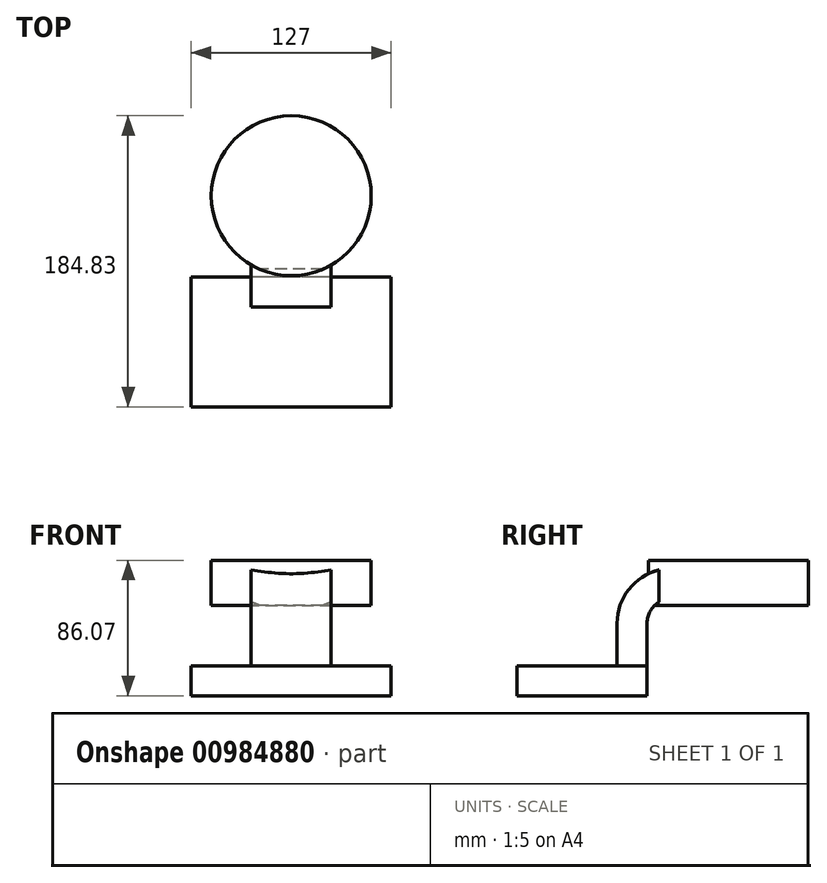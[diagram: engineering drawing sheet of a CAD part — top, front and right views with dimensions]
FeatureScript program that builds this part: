
annotation { "Feature Type Name" : "Feature", "Feature Type Description" : "" }
export const myFeature = defineFeature(function(context is Context, id is Id, definition is map)
    precondition{}
    {
        {
            var Q0;
            Q0=qCreatedBy(makeId("Right.planeOp"),FACE);
            var sketch = newSketch(context, id + "F0", { "sketchPlane" : qUnion([Q0])});
            skLineSegment(sketch, "E0.bottom", {"start": v(-41.28, 9.52) * mm, "end": v(41.28, 9.53) * mm});
            skLineSegment(sketch, "E0.top", {"start": v(-41.27, -9.52) * mm, "end": v(41.28, -9.52) * mm});
            skLineSegment(sketch, "E0.left", {"start": v(-41.28, 9.52) * mm, "end": v(-41.28, -9.52) * mm});
            skLineSegment(sketch, "E0.right", {"start": v(41.27, 9.53) * mm, "end": v(41.28, -9.52) * mm});
            skPoint(sketch, "E0.middle", {"position": v(0, 0) * mm});
            skLineSegment(sketch, "E1.bottom", {"start": v(143.56, 47.96) * mm, "end": v(92.76, 47.96) * mm});
            skLineSegment(sketch, "E1.top", {"start": v(143.56, 76.54) * mm, "end": v(92.76, 76.54) * mm});
            skLineSegment(sketch, "E1.left", {"start": v(143.56, 47.96) * mm, "end": v(143.56, 76.54) * mm});
            skLineSegment(sketch, "E1.right", {"start": v(92.76, 47.96) * mm, "end": v(92.76, 76.54) * mm});
            skPoint(sketch, "E1.middle", {"position": v(118.16, 62.25) * mm});
            skLineSegment(sketch, "E2", {"start": v(41.27, 9.53) * mm, "end": v(41.27, 36.51) * mm});
            skArc(sketch, "E3", {"start": v(41.27, 36.51) * mm, "mid": v(45.92, 47.74) * mm, "end": v(57.15, 52.39) * mm});
            skPoint(sketch, "E4.startSnap0", {"position": v(57.15, 52.39) * mm});
            skLineSegment(sketch, "E5.0", {"start": v(57.15, 71.44) * mm, "end": v(98.42, 71.44) * mm});
            skArc(sketch, "E5.1", {"start": v(22.22, 36.51) * mm, "mid": v(32.45, 61.2) * mm, "end": v(57.15, 71.44) * mm});
            skLineSegment(sketch, "E5.2", {"start": v(22.22, 9.53) * mm, "end": v(22.22, 36.51) * mm});
            skLineSegment(sketch, "E6", {"start": v(57.15, 52.39) * mm, "end": v(98.42, 52.39) * mm});
            skFitSpline(sketch, "E7", {"points": [v(-41.28, 9.52) * mm, v(92.76, 76.54) * mm], "startDerivative": vector(11.45, 249.12) * mm, "endDerivative": vector(278.28, -17.77) * mm});
            skSolve(sketch);
        }
        {
            var Q0;
            Q0=makeQuery(id+"F0.imprint","IMPRINT",FACE,{"disambiguationData":[TD([[makeQuery(id+"F0.imprint","IMPRINT",EDGE,{"derivedFrom":sQuery(id+"F0.wireOp",EDGE,"E0.top")}),1.0]])]});
            extrude(context, id + "F1", {"entities" : qUnion([Q0]), "endBound" : BoundingType.SYMMETRIC, "depth" : 127 * mm, "offsetDistance" : 25.4 * mm});
        }
        {
            var Q0;
            {var subQ1=sQuery(id+"F0.wireOp",EDGE,"E2");Q0=makeQuery(id+"F0.imprint","IMPRINT",FACE,{"disambiguationData":[TD([[makeQuery(id+"F0.imprint","IMPRINT",EDGE,{"derivedFrom":subQ1}),1.0]])]});}
            extrude(context, id + "F2", {"entities" : qUnion([Q0]), "operationType" : NewBodyOperationType.ADD, "endBound" : BoundingType.SYMMETRIC, "depth" : 50.8 * mm, "offsetDistance" : 25.4 * mm});
        }
        {
            var Q0;
            {var subQ0=sQuery(id+"F0.wireOp",EDGE,"E5.1");Q0=makeQuery(id+"F0.imprint","IMPRINT",FACE,{"disambiguationData":[TD([[makeQuery(id+"F0.imprint","IMPRINT",EDGE,{"derivedFrom":subQ0}),1.0]])]});}
            extrude(context, id + "F3", {"entities" : qUnion([Q0]), "operationType" : NewBodyOperationType.ADD, "endBound" : BoundingType.SYMMETRIC, "depth" : 25.4 * mm, "offsetDistance" : 25.4 * mm});
        }
        {
            var Q0;
            {var subQ1=sQuery(id+"F0.wireOp",EDGE,"E1.bottom");Q0=makeQuery(id+"F0.imprint","IMPRINT",FACE,{"disambiguationData":[TD([[makeQuery(id+"F0.imprint","IMPRINT",EDGE,{"derivedFrom":subQ1}),-1.0]])]});}
            var Q1;
            Q1=sQuery(id+"F0.wireOp",EDGE,"E1.right");
            revolve(context, id + "F4", {"operationType" : NewBodyOperationType.ADD, "surfaceOperationType" : NewSurfaceOperationType.NEW, "entities" : qUnion([Q0]), "axis" : qUnion([Q1]), "revolveType" : RevolveType.FULL});
        }
    });
